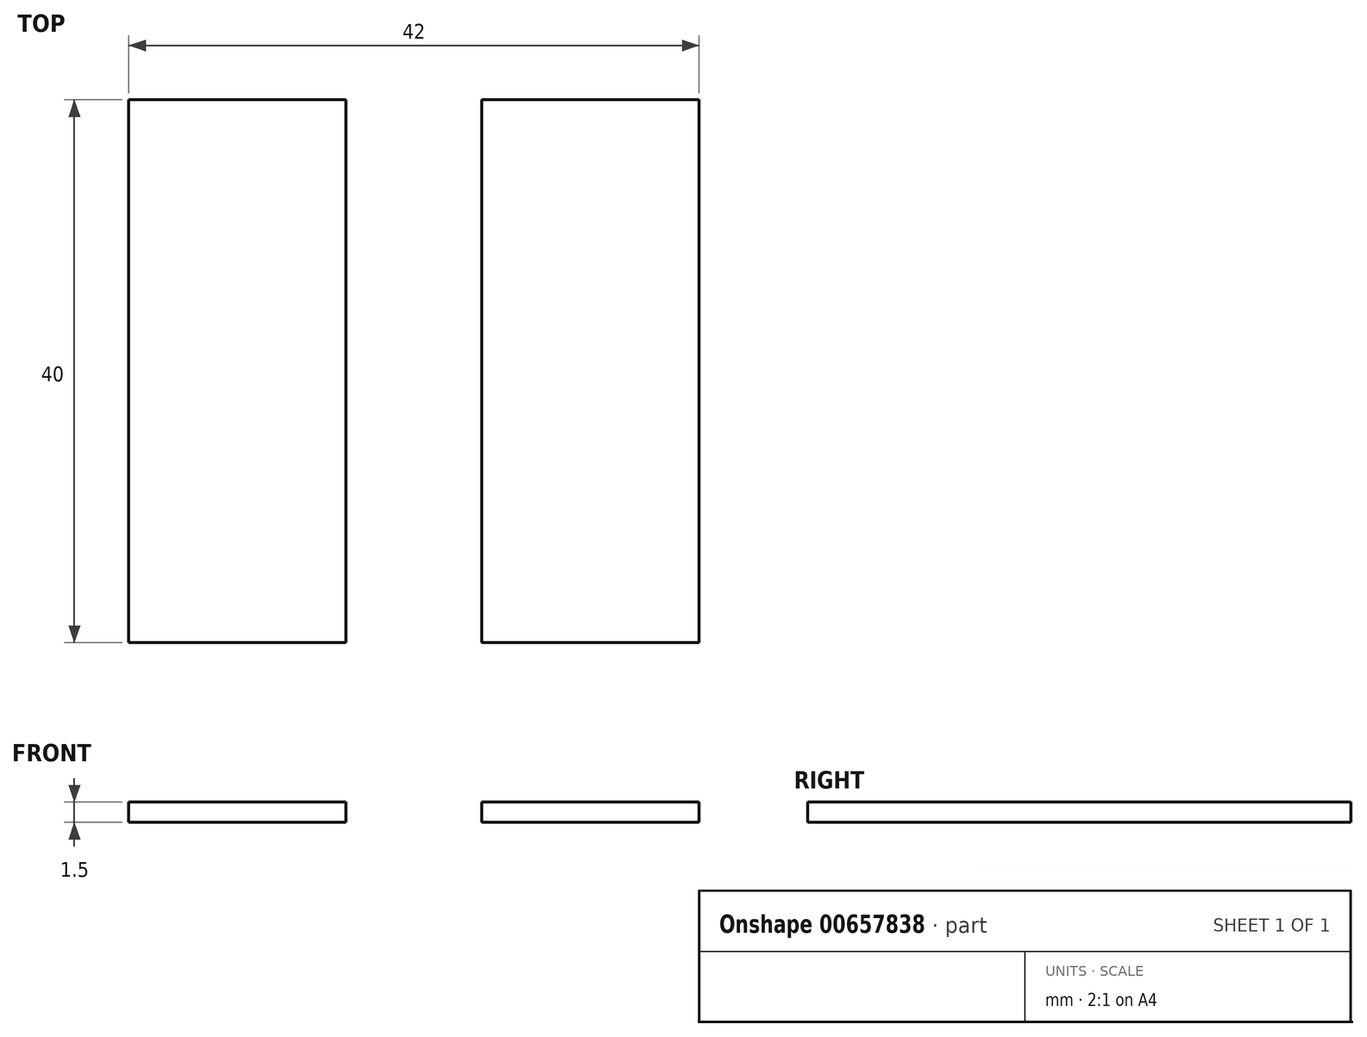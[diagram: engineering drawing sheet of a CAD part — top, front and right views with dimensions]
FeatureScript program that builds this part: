
annotation { "Feature Type Name" : "Feature", "Feature Type Description" : "" }
export const myFeature = defineFeature(function(context is Context, id is Id, definition is map)
    precondition{}
    {
        {
            var Q0;
            Q0=qCreatedBy(makeId("Top.planeOp"),FACE);
            var sketch = newSketch(context, id + "F0", { "sketchPlane" : qUnion([Q0])});
            skLineSegment(sketch, "E0.bottom", {"start": v(-8, 20) * mm, "end": v(8, 20) * mm});
            skLineSegment(sketch, "E0.top", {"start": v(-8, -20) * mm, "end": v(8, -20) * mm});
            skLineSegment(sketch, "E0.left", {"start": v(-8, 20) * mm, "end": v(-8, -20) * mm});
            skLineSegment(sketch, "E0.right", {"start": v(8, 20) * mm, "end": v(8, -20) * mm});
            skLineSegment(sketch, "E1.bottom", {"start": v(-18, 20) * mm, "end": v(-34, 20) * mm});
            skLineSegment(sketch, "E1.top", {"start": v(-18, -20) * mm, "end": v(-34, -20) * mm});
            skLineSegment(sketch, "E1.left", {"start": v(-18, 20) * mm, "end": v(-18, -20) * mm});
            skLineSegment(sketch, "E1.right", {"start": v(-34, 20) * mm, "end": v(-34, -20) * mm});
            skLineSegment(sketch, "E2.bottom", {"start": v(18, 20) * mm, "end": v(34, 20) * mm});
            skLineSegment(sketch, "E2.top", {"start": v(18, -20) * mm, "end": v(34, -20) * mm});
            skLineSegment(sketch, "E2.left", {"start": v(18, 20) * mm, "end": v(18, -20) * mm});
            skLineSegment(sketch, "E2.right", {"start": v(34, 20) * mm, "end": v(34, -20) * mm});
            skSolve(sketch);
        }
        {
            var Q0;
            Q0=makeQuery(id+"F0.imprint","IMPRINT",FACE,{"disambiguationData":[TD([[makeQuery(id+"F0.imprint","IMPRINT",EDGE,{"derivedFrom":sQuery(id+"F0.wireOp",EDGE,"E1.bottom")}),1.0]])]});
            extrude(context, id + "F1", {"entities" : qUnion([Q0]), "depth" : 1.5 * mm});
        }
        {
            var Q0;
            Q0=makeQuery(id+"F0.imprint","IMPRINT",FACE,{"disambiguationData":[TD([[makeQuery(id+"F0.imprint","IMPRINT",EDGE,{"derivedFrom":sQuery(id+"F0.wireOp",EDGE,"E0.bottom")}),-1.0]])]});
            extrude(context, id + "F2", {"entities" : qUnion([Q0]), "depth" : 1.5 * mm});
        }
        {
            var Q0;
            Q0=makeQuery(id+"F0.imprint","IMPRINT",FACE,{"disambiguationData":[TD([[makeQuery(id+"F0.imprint","IMPRINT",EDGE,{"derivedFrom":sQuery(id+"F0.wireOp",EDGE,"E2.bottom")}),-1.0]])]});
            extrude(context, id + "F3", {"entities" : qUnion([Q0]), "depth" : 1.5 * mm});
        }
        {
            var Q0;
            Q0=makeQuery(id+"F3.opExtrude","SWEPT_BODY",BODY,{"disambiguationData":[OSD([sQuery(id+"F0.wireOp",EDGE,"E2.bottom"),sQuery(id+"F0.wireOp",EDGE,"E2.top"),sQuery(id+"F0.wireOp",EDGE,"E2.left"),sQuery(id+"F0.wireOp",EDGE,"E2.right")])]});
            deleteBodies(context, id + "F4", {"entities" : qUnion([Q0])});
        }
    });
